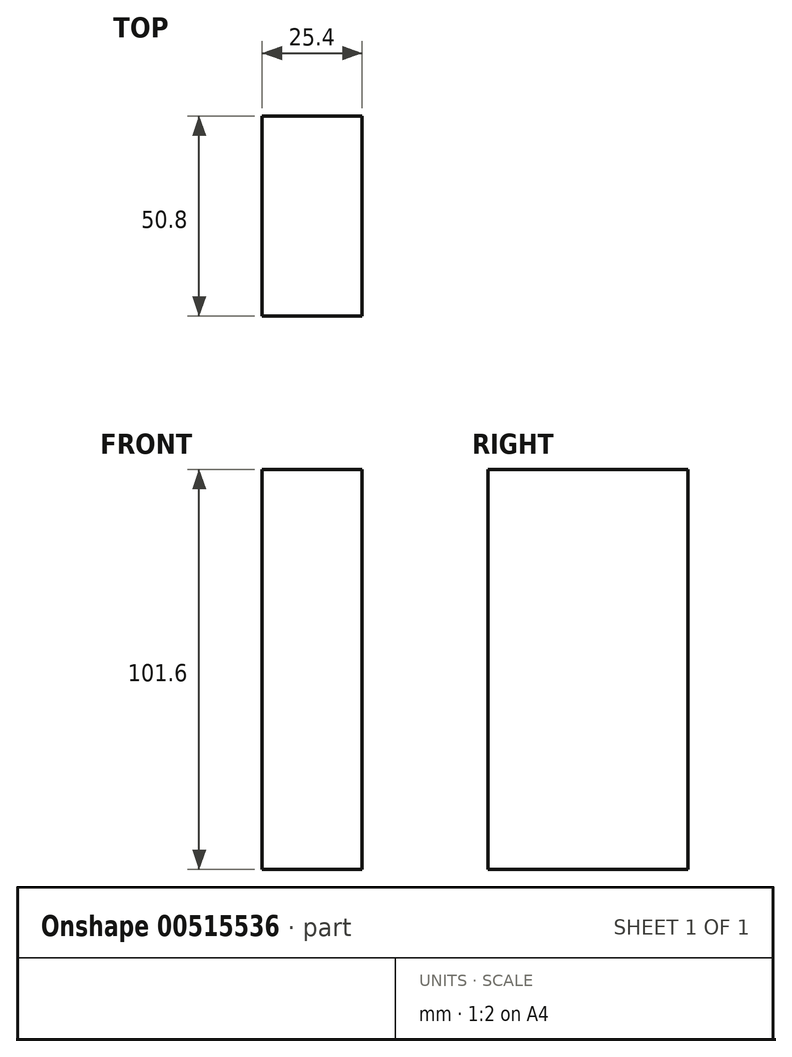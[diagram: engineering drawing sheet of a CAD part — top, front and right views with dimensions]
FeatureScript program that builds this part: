
annotation { "Feature Type Name" : "Feature", "Feature Type Description" : "" }
export const myFeature = defineFeature(function(context is Context, id is Id, definition is map)
    precondition{}
    {
        {
            var Q0;
            Q0=qCreatedBy(makeId("Right.planeOp"),FACE);
            var sketch = newSketch(context, id + "F0", { "sketchPlane" : qUnion([Q0])});
            skLineSegment(sketch, "E0.bottom", {"start": v(0, 0) * mm, "end": v(-50.8, 0) * mm});
            skLineSegment(sketch, "E0.top", {"start": v(0, 101.6) * mm, "end": v(-50.8, 101.6) * mm});
            skLineSegment(sketch, "E0.left", {"start": v(0, 0) * mm, "end": v(0, 101.6) * mm});
            skLineSegment(sketch, "E0.right", {"start": v(-50.8, 0) * mm, "end": v(-50.8, 101.6) * mm});
            skSolve(sketch);
        }
        {
            var Q0;
            Q0=makeQuery(id+"F0.imprint","IMPRINT",FACE,{"disambiguationData":[TD([[makeQuery(id+"F0.imprint","IMPRINT",EDGE,{"derivedFrom":sQuery(id+"F0.wireOp",EDGE,"E0.bottom")}),-1.0]])]});
            extrude(context, id + "F1", {"entities" : qUnion([Q0]), "depth" : 25.4 * mm, "offsetDistance" : 25.4 * mm});
        }
    });
